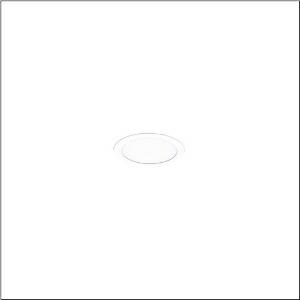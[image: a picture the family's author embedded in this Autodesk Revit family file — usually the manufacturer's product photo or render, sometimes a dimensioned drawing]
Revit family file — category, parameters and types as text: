
# Revit family: lunis_21_s_51db16ea91c
name_source: partatom
category: Lighting Fixtures
units: mm (PartAtom-declared; Revit-internal decimal feet)

## family parameters
Cut with Voids When Loaded = No
Host = Face
Light Source = No
Part Type = Normal
Room Calculation Point = No
Round Connector Dimension = Use Diameter
Shared = No

## types (1)
- --- (1 x LED, 1000 lm, 8 W, 6500K)
    Apparent Load = 8 VA
    CIE Flux Codes = 50 80 96 100 100
    Color Rendering = 80
    Color Temperature = 6500K
    Default Elevation = 1800 mm
    Description = Lunis 21,  S, downlight, light control with lens, of PMMA, optical cover: cover panel, of PC, opal, light emission: direct distribution, LED rated luminous flux: 770lm, light colour: 830/840/865, with terminal, 5-pole, mains connection: 220..240V, AC, 50..60Hz, housing, round, of diecast aluminium, traffic white (RAL 9016), diameter: 84mm, clamping range: 1..40mm, protection rating (complete): IP20, protection rating (on room side): IP54, insulation class (complete): insulation class II (safety insulation), certification: CE, impact resistance: IK03, packaging unit: 1 piece
    Height = 0 mm  [stored 0 ft]
    Lamp = 1 x LED
    Lamp Light Flux = 1000 lm
    Lamp Power = 8 W
    Lamp count = 1
    Length = 84 mm
    Luminous efficacy = 125 lm/W
    Manufacturer = Siteco
    ModVariant = No
    Model = 51DB16EA91C
    Mounting Place = Ceiling
    Mounting Type = Recessed
    Number of Poles = 1
    OnlyDefault = Yes
    Power Factor = 1
    Product Name = Lunis 21 S
    Product group = downlight
    ProductGroupID = 400
    Protection Class = Protection class II
    Protection Degree = IP 20
    RLX_Detail_Level = 1
    RLX_Emergency_Light_Flux = 0 lm
    RLX_Emergency_Type = 0
    RLX_Emergency_Type_DB = No
    RlxData = <blob elided: 8729 chars, md5=768e3c30>
    Socket = socket
    Standby Power = 0 W
    System Light Flux = 1000 lm
    System Power = 8 W
    Type Comments = individual setting: colour temperature 6500K, luminous flux: 100 % | (OFF | OFF | ON | OFF) | 200 mA
    Type Image = l_1290838.jpg
    URL = http://relux.com
    VarID = @adj_018592
    Voltage = 0 V
    Weight = 0.00 kg
    Width = 0 mm  [stored 0 ft]

note: [stored X ft] marks values corroborated as IEEE doubles in the binary element streams (Revit-internal decimal feet)

## geometry (parser evidence)
native form markers: Sweep x9
no freeform markers — native parametric forms only
